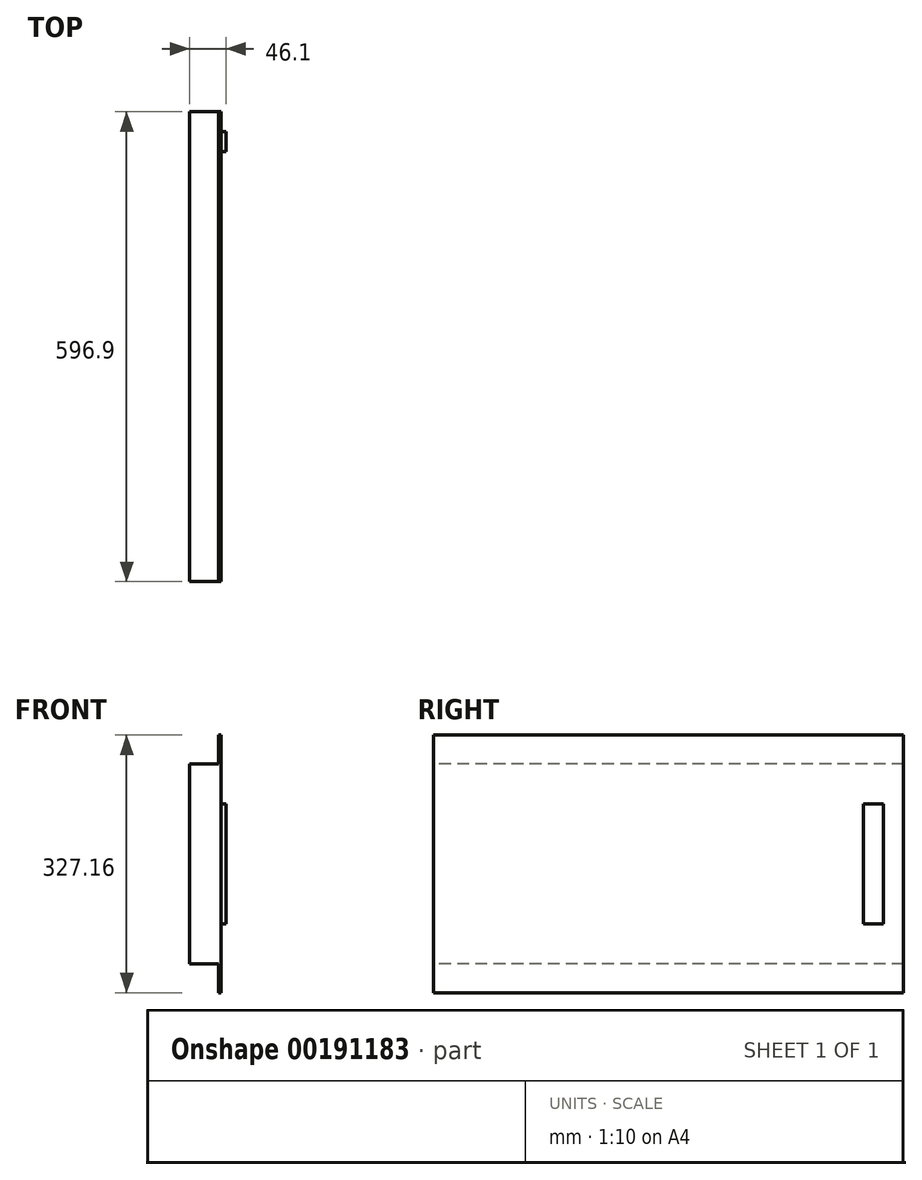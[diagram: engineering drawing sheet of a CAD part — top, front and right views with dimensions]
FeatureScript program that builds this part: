
annotation { "Feature Type Name" : "Feature", "Feature Type Description" : "" }
export const myFeature = defineFeature(function(context is Context, id is Id, definition is map)
    precondition{}
    {
        {
            var Q0;
            Q0=qCreatedBy(makeId("Right.planeOp"),FACE);
            var sketch = newSketch(context, id + "F0", { "sketchPlane" : qUnion([Q0])});
            skLineSegment(sketch, "E0.bottom", {"start": v(298.45, -127) * mm, "end": v(-298.45, -127) * mm});
            skLineSegment(sketch, "E0.top", {"start": v(298.45, 127) * mm, "end": v(-298.45, 127) * mm});
            skLineSegment(sketch, "E0.left", {"start": v(298.45, -127) * mm, "end": v(298.45, 127) * mm});
            skLineSegment(sketch, "E0.right", {"start": v(-298.45, -127) * mm, "end": v(-298.45, 127) * mm});
            skPoint(sketch, "E0.middle", {"position": v(0, 0) * mm});
            skSolve(sketch);
        }
        {
            var Q0;
            Q0=qSketchRegion(id+"F0",true);
            extrude(context, id + "F1", {"entities" : qUnion([Q0]), "depth" : 36.58 * mm});
        }
        {
            var Q0;
            Q0=makeQuery(id+"F1.opExtrude","CAP_FACE",FACE,{"disambiguationData":[OSD([sQuery(id+"F0.wireOp",EDGE,"E0.bottom"),sQuery(id+"F0.wireOp",EDGE,"E0.top"),sQuery(id+"F0.wireOp",EDGE,"E0.left"),sQuery(id+"F0.wireOp",EDGE,"E0.right")])],"isStart":false});
            var sketch = newSketch(context, id + "F2", { "sketchPlane" : qUnion([Q0])});
            skLineSegment(sketch, "E1.top", {"start": v(-298.45, -163.58) * mm, "end": v(298.45, -163.58) * mm});
            skLineSegment(sketch, "E1.left", {"start": v(-298.45, 163.58) * mm, "end": v(-298.45, -163.58) * mm});
            skLineSegment(sketch, "E1.right", {"start": v(298.45, 163.58) * mm, "end": v(298.45, -163.58) * mm});
            skLineSegment(sketch, "E2.0", {"start": v(298.45, 163.58) * mm, "end": v(-298.45, 163.58) * mm});
            skSolve(sketch);
        }
        {
            var Q0;
            Q0 = qSketchRegion(id + "F2", true);
            extrude(context, id + "F3", {"entities" : qUnion([Q0]), "operationType" : NewBodyOperationType.ADD, "depth" : 3.17 * mm});
        }
        {
            var Q0;
            Q0=makeQuery(id+"F3.opExtrude","CAP_FACE",FACE,{"disambiguationData":[OSD([sQuery(id+"F2.wireOp",EDGE,"E1.bottom"),sQuery(id+"F2.wireOp",EDGE,"E1.top"),sQuery(id+"F2.wireOp",EDGE,"E1.left"),sQuery(id+"F2.wireOp",EDGE,"E1.right")])],"isStart":false});
            var sketch = newSketch(context, id + "F4", { "sketchPlane" : qUnion([Q0])});
            skLineSegment(sketch, "E3.bottom", {"start": v(273.05, 76.2) * mm, "end": v(247.65, 76.2) * mm});
            skLineSegment(sketch, "E3.top", {"start": v(273.05, -76.2) * mm, "end": v(247.65, -76.2) * mm});
            skLineSegment(sketch, "E3.left", {"start": v(273.05, 76.2) * mm, "end": v(273.05, -76.2) * mm});
            skLineSegment(sketch, "E3.right", {"start": v(247.65, 76.2) * mm, "end": v(247.65, -76.2) * mm});
            skPoint(sketch, "E3.middle", {"position": v(260.35, 0) * mm});
            skSolve(sketch);
        }
        {
            var Q0;
            Q0 = qSketchRegion(id + "F4", true);
            extrude(context, id + "F5", {"entities" : qUnion([Q0]), "operationType" : NewBodyOperationType.ADD, "depth" : 6.35 * mm});
        }
    });
